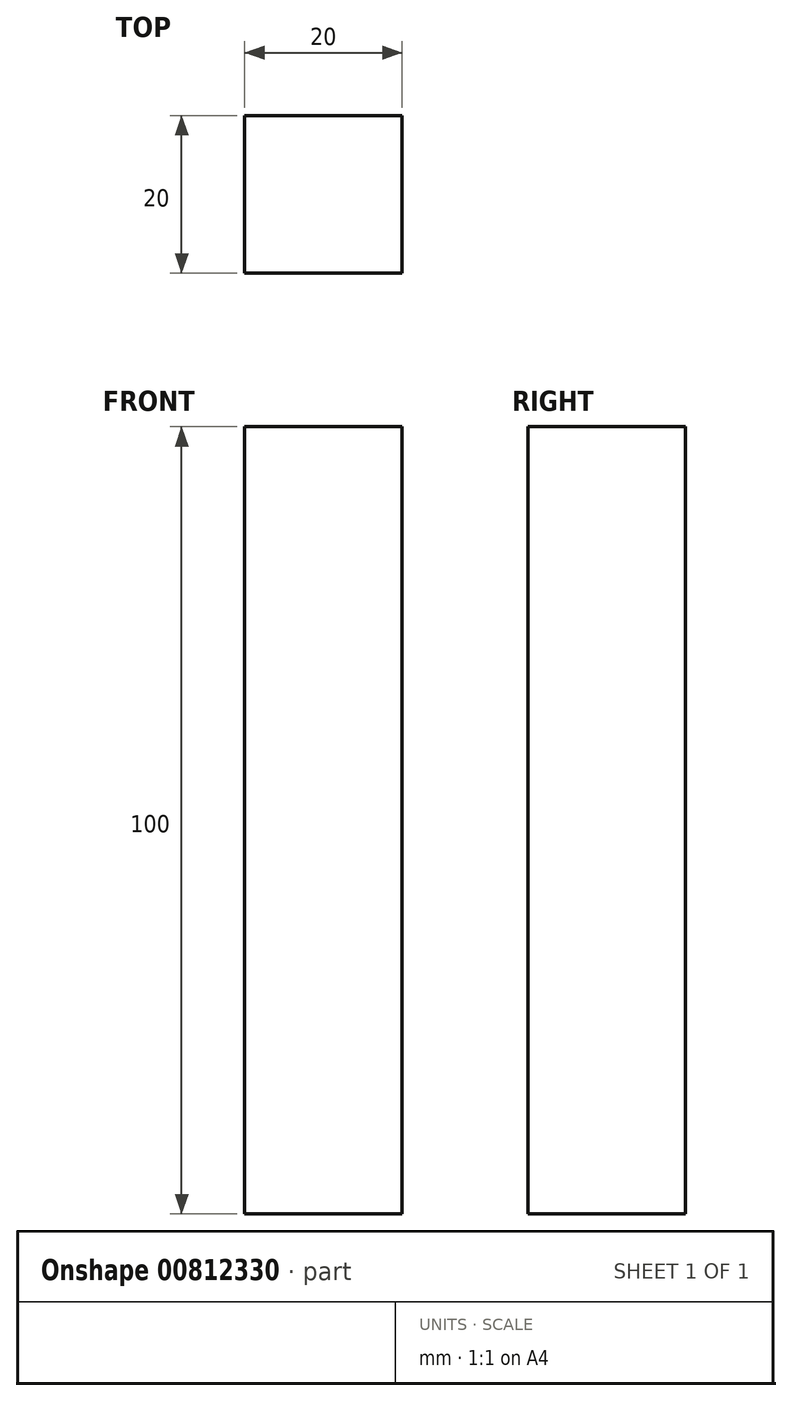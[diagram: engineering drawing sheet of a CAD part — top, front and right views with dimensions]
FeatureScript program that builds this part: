
annotation { "Feature Type Name" : "Feature", "Feature Type Description" : "" }
export const myFeature = defineFeature(function(context is Context, id is Id, definition is map)
    precondition{}
    {
        {
            var Q0;
            Q0=qCreatedBy(makeId("Top.planeOp"),FACE);
            var sketch = newSketch(context, id + "F0", { "sketchPlane" : qUnion([Q0])});
            skLineSegment(sketch, "E0.bottom", {"start": v(-10, 10) * mm, "end": v(10, 10) * mm});
            skLineSegment(sketch, "E0.top", {"start": v(-10, -10) * mm, "end": v(10, -10) * mm});
            skLineSegment(sketch, "E0.left", {"start": v(-10, 10) * mm, "end": v(-10, -10) * mm});
            skLineSegment(sketch, "E0.right", {"start": v(10, 10) * mm, "end": v(10, -10) * mm});
            skSolve(sketch);
        }
        {
            var Q0;
            Q0=makeQuery(id+"F0.imprint","IMPRINT",FACE,{"disambiguationData":[TD([[makeQuery(id+"F0.imprint","IMPRINT",EDGE,{"derivedFrom":sQuery(id+"F0.wireOp",EDGE,"E0.bottom")}),-1.0]])]});
            extrude(context, id + "F1", {"entities" : qUnion([Q0]), "depth" : 100 * mm, "offsetDistance" : 25 * mm});
        }
    });
